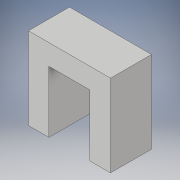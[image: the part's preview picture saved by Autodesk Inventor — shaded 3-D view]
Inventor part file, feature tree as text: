
AUTODESK INVENTOR PART (.ipt)
format: ipt  version: 2017 (Build 210142000, 142)  size: 92,672 bytes
history: native  units: in
note: dims shown in document units (in); Inventor stores cm internally (conversion verified against a paired STEP export)
features: extrude x1, sketch x1
ambient origin geometry x8: Origin, YZ Plane, XZ Plane, XY Plane, X Axis, Y Axis, Z Axis, Center Point
bodies: Solid1 (feature_tree)
feature tree (2):
  extrude  "Extrusion1"  Depth=1.0in
  sketch  "Sketch1"  dims[d0=1.0in d1=1.0in d2=0.25in d3=0.75in d4=0.5in d5=0.5in d6=0.0in]
